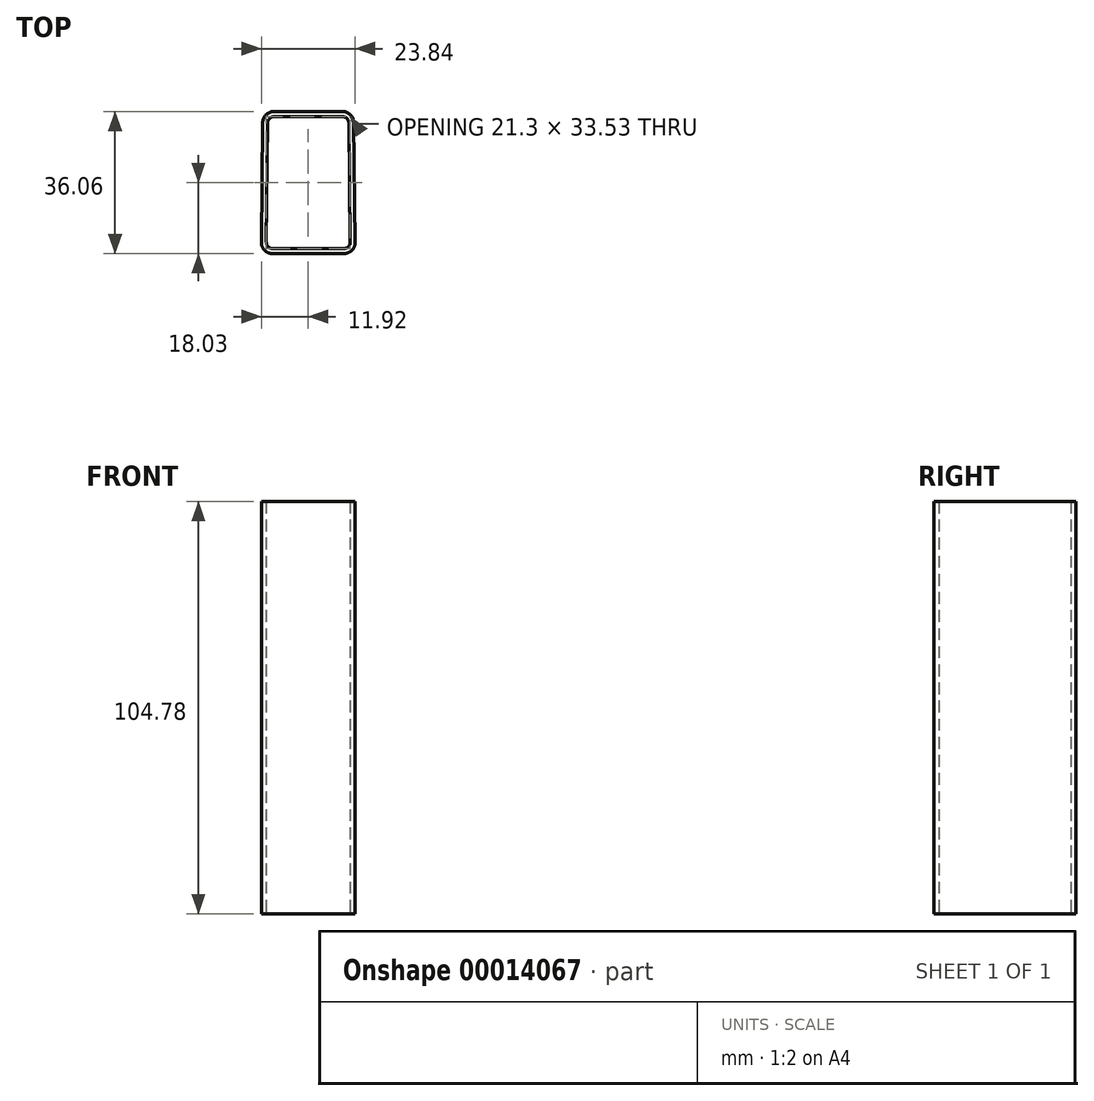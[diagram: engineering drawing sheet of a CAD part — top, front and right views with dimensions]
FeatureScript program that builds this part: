
annotation { "Feature Type Name" : "Feature", "Feature Type Description" : "" }
export const myFeature = defineFeature(function(context is Context, id is Id, definition is map)
    precondition{}
    {
        {
            var Q0;
            Q0=qCreatedBy(makeId("Top.planeOp"),FACE);
            var sketch = newSketch(context, id + "F0", { "sketchPlane" : qUnion([Q0])});
            skLineSegment(sketch, "E0", {"start": v(-8.72, 16.76) * mm, "end": v(8.72, 16.76) * mm});
            skLineSegment(sketch, "E1", {"start": v(10.3, 15.2) * mm, "end": v(10.65, -15.16) * mm});
            skLineSegment(sketch, "E2", {"start": v(9.06, -16.76) * mm, "end": v(-9.06, -16.76) * mm});
            skLineSegment(sketch, "E3", {"start": v(-10.65, -15.16) * mm, "end": v(-10.3, 15.2) * mm});
            skLineSegment(sketch, "E4", {"start": v(0, 16.76) * mm, "end": v(0, -16.76) * mm, "construction": true});
            skPoint(sketch, "E5.visualSharp", {"position": v(-10.29, 16.76) * mm});
            skArc(sketch, "E5.filletArc", {"start": v(-8.72, 16.76) * mm, "mid": v(-9.83, 16.3) * mm, "end": v(-10.3, 15.2) * mm});
            skPoint(sketch, "E6.visualSharp", {"position": v(10.29, 16.76) * mm});
            skArc(sketch, "E6.filletArc", {"start": v(10.3, 15.2) * mm, "mid": v(9.83, 16.3) * mm, "end": v(8.72, 16.76) * mm});
            skPoint(sketch, "E7.visualSharp", {"position": v(10.67, -16.76) * mm});
            skArc(sketch, "E7.filletArc", {"start": v(9.06, -16.76) * mm, "mid": v(10.2, -16.3) * mm, "end": v(10.65, -15.16) * mm});
            skPoint(sketch, "E8.visualSharp", {"position": v(-10.67, -16.76) * mm});
            skArc(sketch, "E8.filletArc", {"start": v(-10.65, -15.16) * mm, "mid": v(-10.2, -16.3) * mm, "end": v(-9.06, -16.76) * mm});
            skArc(sketch, "E9.0", {"start": v(9.06, -18.03) * mm, "mid": v(11.1, -17.19) * mm, "end": v(11.92, -15.14) * mm});
            skLineSegment(sketch, "E9.1", {"start": v(11.57, 15.2) * mm, "end": v(11.92, -15.14) * mm});
            skArc(sketch, "E9.2", {"start": v(11.57, 15.2) * mm, "mid": v(10.73, 17.2) * mm, "end": v(8.72, 18.03) * mm});
            skLineSegment(sketch, "E9.3", {"start": v(-8.72, 18.03) * mm, "end": v(8.72, 18.03) * mm});
            skArc(sketch, "E9.4", {"start": v(-8.72, 18.03) * mm, "mid": v(-10.73, 17.2) * mm, "end": v(-11.57, 15.2) * mm});
            skLineSegment(sketch, "E9.5", {"start": v(9.06, -18.03) * mm, "end": v(-9.06, -18.03) * mm});
            skLineSegment(sketch, "E9.6", {"start": v(-11.92, -15.14) * mm, "end": v(-11.57, 15.2) * mm});
            skArc(sketch, "E9.7", {"start": v(-11.92, -15.14) * mm, "mid": v(-11.1, -17.19) * mm, "end": v(-9.06, -18.03) * mm});
            skSolve(sketch);
        }
        {
            var Q0;
            Q0=makeQuery(id+"F0.imprint","IMPRINT",FACE,{"disambiguationData":[TD([[makeQuery(id+"F0.imprint","IMPRINT",EDGE,{"derivedFrom":sQuery(id+"F0.wireOp",EDGE,"E0")}),1.0]])]});
            extrude(context, id + "F1", {"entities" : qUnion([Q0]), "endBound" : BoundingType.SYMMETRIC, "depth" : 104.77 * mm});
        }
    });
